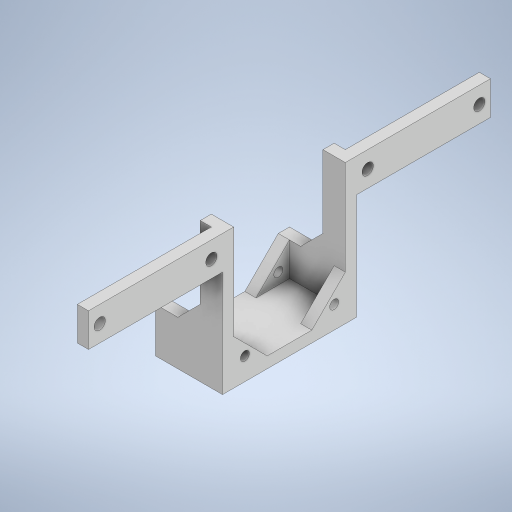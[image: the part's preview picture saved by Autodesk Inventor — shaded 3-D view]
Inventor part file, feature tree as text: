
AUTODESK INVENTOR PART (.ipt)
format: ipt  version: 2023 (Build 270158000, 158)  size: 346,624 bytes
history: native  units: mm
features: extrude x8, sketch x8, mirror x2
ambient origin geometry x8: Origin, YZ Plane, XZ Plane, XY Plane, X Axis, Y Axis, Z Axis, Center Point
bodies: Solid1 (feature_tree)
feature tree (18):
  extrude  "Extrusion1"  TaperAngle=45.0deg  [1 undecoded]
  extrude  "Extrusion2"  Depth=5.0mm
  mirror  "Mirror1"
  extrude  "Extrusion5"  Depth=20.0mm
  extrude  "Extrusion6"  Depth=15.0mm
  extrude  "Extrusion8"  Depth=10.0mm TaperAngle=0.0deg
  mirror  "Mirror2"
  extrude  "Extrusion7"  Depth=2.0mm TaperAngle=0.0deg
  extrude  "Extrusion3"  TaperAngle=0.0deg  [1 undecoded]
  extrude  "Extrusion4"  Depth=62.5mm TaperAngle=0.0deg
  sketch  "Sketch1"  dims[d0=50.0mm d1=45.0deg]
  sketch  "Sketch2"  dims[d2=5.0mm d4=40.0mm]
  sketch  "Sketch3"  dims[d5=4.0mm d6=20.0mm]
  sketch  "Sketch4"  dims[d7=5.0mm d8=15.0mm]
  sketch  "Sketch5"  dims[d9=5.0mm d10=0.0mm d11=10.0mm d12=0.0mm]
  sketch  "Sketch6"  dims[d13=6.0mm d14=2.0mm d15=0.0mm]
  sketch  "Sketch7"  dims[d16=4.0mm d17=0.0mm d18=0.0mm]
  sketch  "Sketch8"  dims[d19=5.0mm d20=62.5mm d21=0.0mm d23=60.0mm d24=0.0mm d25=5.0mm d26=15.0mm d29=0.0mm d30=0.0mm d31=5.0mm d32=5.0mm d33=5.0mm d34=10.0mm d35=0.0mm d38=5.0mm d39=45.0deg d40=10.0mm]
note: 2 required parameter values undecoded (feature->parameter linkage not recoverable at this tier; creation-order binding heuristic only, values carry confidence <= 0.55)
